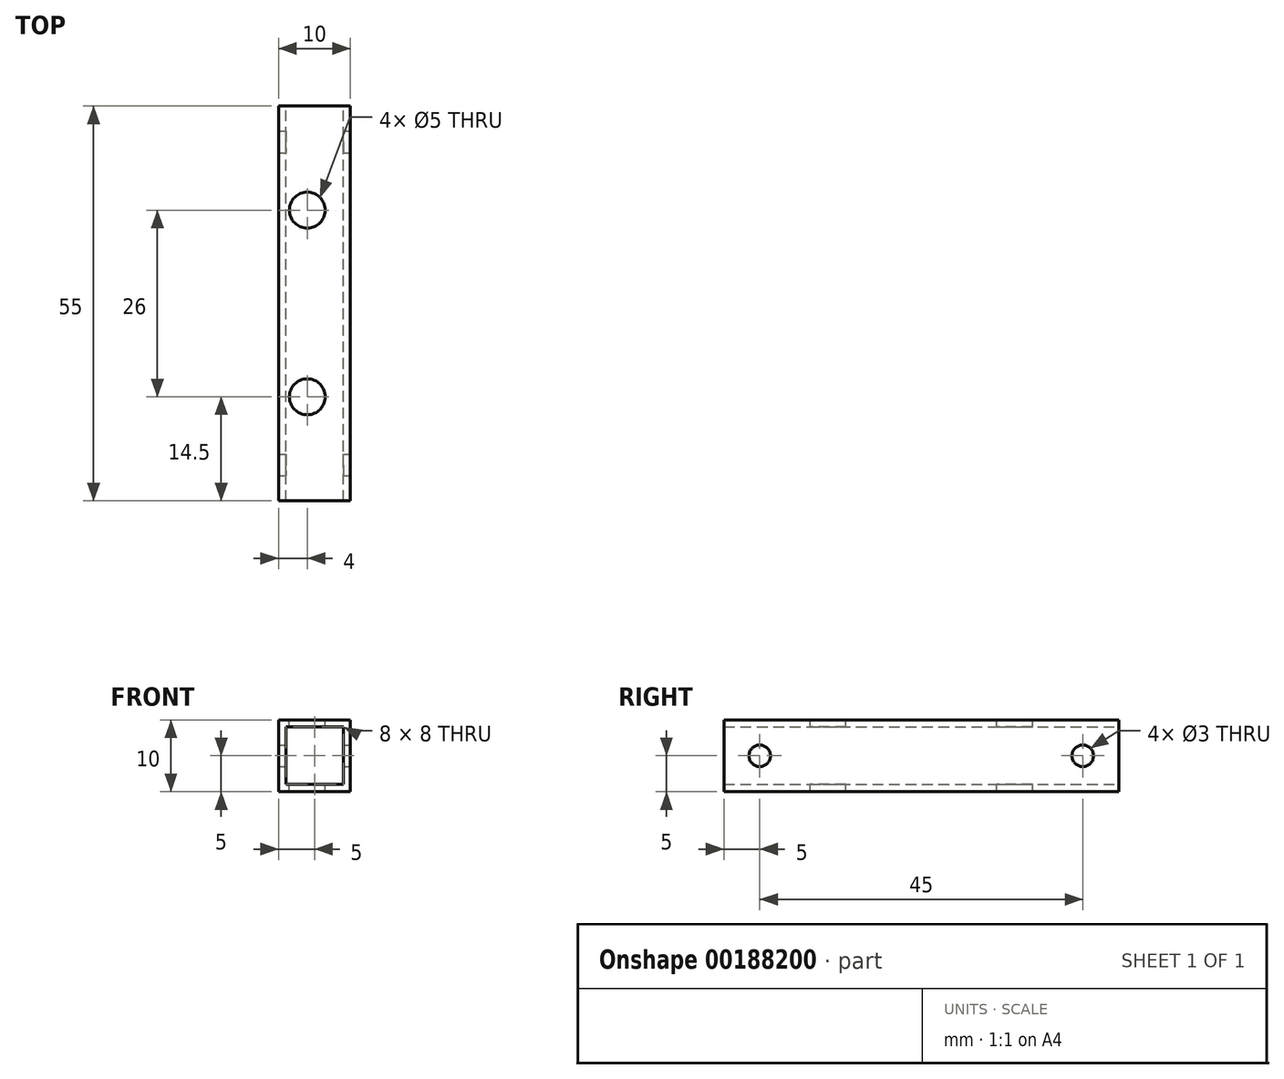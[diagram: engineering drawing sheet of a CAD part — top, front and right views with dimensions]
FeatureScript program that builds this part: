
annotation { "Feature Type Name" : "Feature", "Feature Type Description" : "" }
export const myFeature = defineFeature(function(context is Context, id is Id, definition is map)
    precondition{}
    {
        {
            var Q0;
            Q0=qCreatedBy(makeId("Front.planeOp"),FACE);
            var sketch = newSketch(context, id + "F0", { "sketchPlane" : qUnion([Q0])});
            skLineSegment(sketch, "E0.bottom", {"start": v(-5, -5) * mm, "end": v(5, -5) * mm});
            skLineSegment(sketch, "E0.top", {"start": v(-5, 5) * mm, "end": v(5, 5) * mm});
            skLineSegment(sketch, "E0.left", {"start": v(-5, -5) * mm, "end": v(-5, 5) * mm});
            skLineSegment(sketch, "E0.right", {"start": v(5, -5) * mm, "end": v(5, 5) * mm});
            skPoint(sketch, "E0.middle", {"position": v(0, 0) * mm});
            skLineSegment(sketch, "E1.bottom", {"start": v(-4, -4) * mm, "end": v(4, -4) * mm});
            skLineSegment(sketch, "E1.top", {"start": v(-4, 4) * mm, "end": v(4, 4) * mm});
            skLineSegment(sketch, "E1.left", {"start": v(-4, -4) * mm, "end": v(-4, 4) * mm});
            skLineSegment(sketch, "E1.right", {"start": v(4, -4) * mm, "end": v(4, 4) * mm});
            skSolve(sketch);
        }
        {
            var Q0;
            Q0 = qSketchRegion(id + "F0", true);
            extrude(context, id + "F1", {"entities" : qUnion([Q0]), "depth" : 55 * mm});
        }
        {
            var Q0;
            Q0=makeQuery(id+"F1.opExtrude","SWEPT_FACE",FACE,{"disambiguationData":[OSD([sQuery(id+"F0.wireOp",EDGE,"E0.right")])]});
            var sketch = newSketch(context, id + "F2", { "sketchPlane" : qUnion([Q0])});
            skLineSegment(sketch, "E2", {"start": v(-55, 0) * mm, "end": v(0, 0) * mm, "construction": true});
            skLineSegment(sketch, "E3", {"start": v(-27.5, 5) * mm, "end": v(-27.5, -5) * mm, "construction": true});
            skCircle(sketch, "E4", {"center": v(-50, 0) * mm, "radius": 1.5 * mm});
            skCircle(sketch, "E5.MirrorC", {"center": v(-5, 0) * mm, "radius": 1.5 * mm});
            skSolve(sketch);
        }
        {
            var Q0;
            Q0 = qSketchRegion(id + "F2", true);
            extrude(context, id + "F3", {"entities" : qUnion([Q0]), "operationType" : NewBodyOperationType.REMOVE, "oppositeDirection" : true, "depth" : 25 * mm});
        }
        {
            var Q0;
            Q0=makeQuery(id+"F1.opExtrude","SWEPT_FACE",FACE,{"disambiguationData":[OSD([sQuery(id+"F0.wireOp",EDGE,"E0.top")])]});
            var sketch = newSketch(context, id + "F4", { "sketchPlane" : qUnion([Q0])});
            skLineSegment(sketch, "E6", {"start": v(-1, -55) * mm, "end": v(-1, 0) * mm, "construction": true});
            skLineSegment(sketch, "E7", {"start": v(-5, -27.5) * mm, "end": v(5, -27.5) * mm, "construction": true});
            skCircle(sketch, "E8", {"center": v(-1, -40.5) * mm, "radius": 2.5 * mm});
            skCircle(sketch, "E9.MirrorC", {"center": v(-1, -14.5) * mm, "radius": 2.5 * mm});
            skSolve(sketch);
        }
        {
            var Q0;
            Q0 = qSketchRegion(id + "F4", true);
            extrude(context, id + "F5", {"entities" : qUnion([Q0]), "operationType" : NewBodyOperationType.REMOVE, "oppositeDirection" : true, "depth" : 25 * mm});
        }
    });
